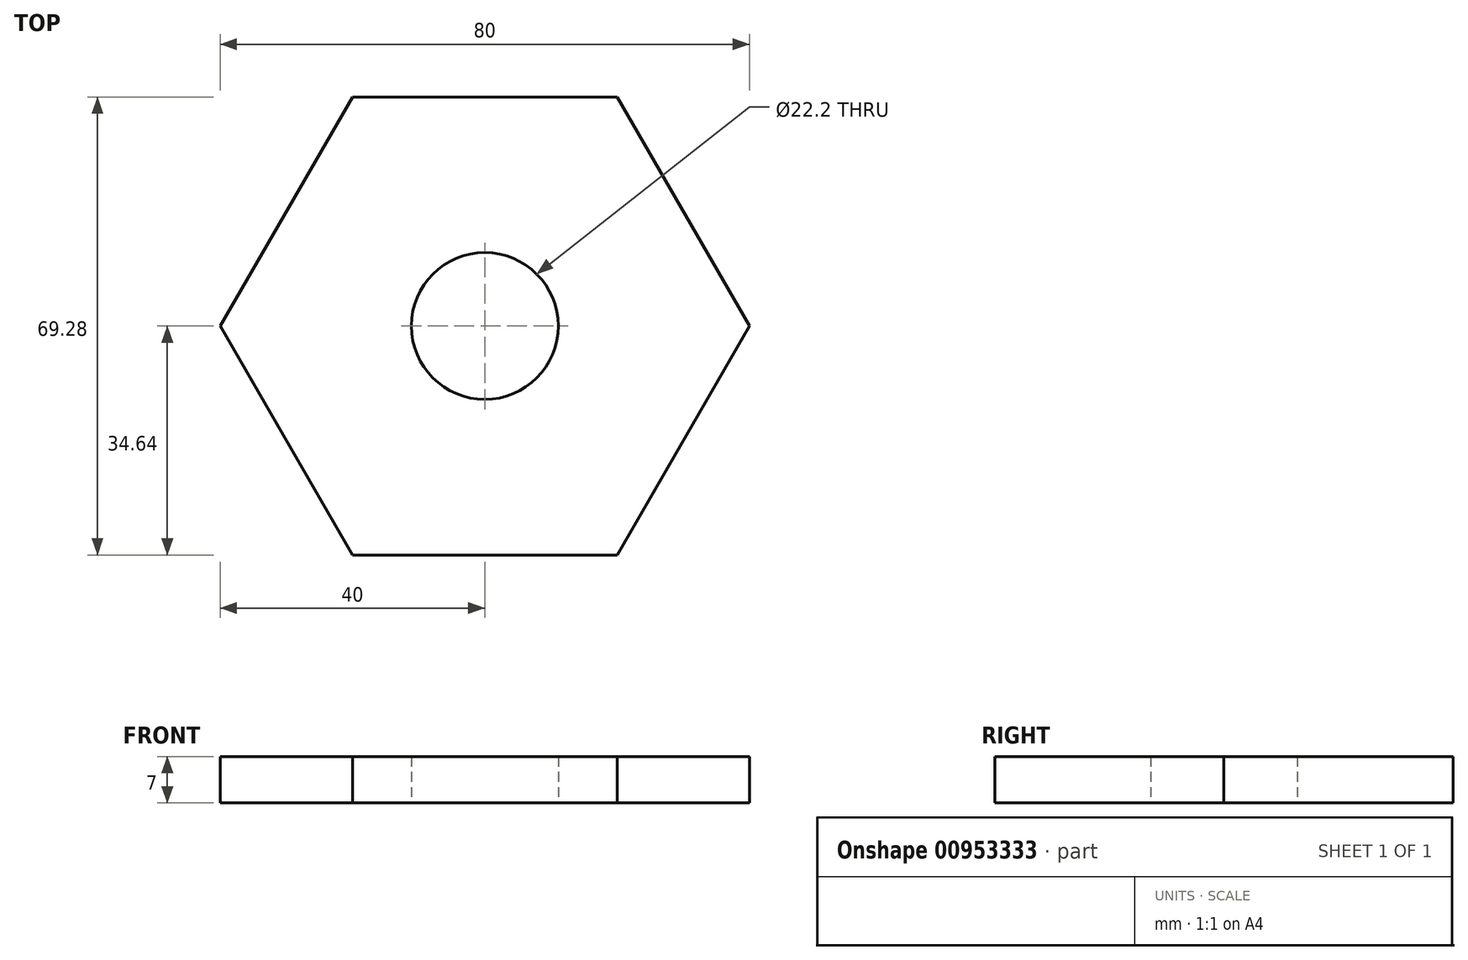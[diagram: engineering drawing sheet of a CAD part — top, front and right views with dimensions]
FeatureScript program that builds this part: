
annotation { "Feature Type Name" : "Feature", "Feature Type Description" : "" }
export const myFeature = defineFeature(function(context is Context, id is Id, definition is map)
    precondition{}
    {
        {
            var Q0;
            Q0=qCreatedBy(makeId("Top.planeOp"),FACE);
            var sketch = newSketch(context, id + "F0", { "sketchPlane" : qUnion([Q0])});
            skCircle(sketch, "E0", {"center": v(0, 0) * mm, "radius": 11.1 * mm});
            skCircle(sketch, "E1.cCircle", {"center": v(0, 0) * mm, "radius": 40 * mm, "construction": true});
            skLineSegment(sketch, "E1.0", {"start": v(40, 0) * mm, "end": v(20, -34.64) * mm});
            skLineSegment(sketch, "E1.1", {"start": v(20, -34.64) * mm, "end": v(-20, -34.64) * mm});
            skLineSegment(sketch, "E1.2", {"start": v(-20, -34.64) * mm, "end": v(-40, 0) * mm});
            skLineSegment(sketch, "E1.3", {"start": v(-40, 0) * mm, "end": v(-20, 34.64) * mm});
            skLineSegment(sketch, "E1.4", {"start": v(-20, 34.64) * mm, "end": v(20, 34.64) * mm});
            skLineSegment(sketch, "E1.5", {"start": v(20, 34.64) * mm, "end": v(40, 0) * mm});
            skLineSegment(sketch, "E2.0", {"start": v(34.5, 3.17) * mm, "end": v(14.5, -31.47) * mm});
            skSolve(sketch);
        }
        {
            var Q0;
            Q0=makeQuery(id+"F0.imprint","IMPRINT",FACE,{"disambiguationData":[TD([[makeQuery(id+"F0.imprint","IMPRINT",EDGE,{"derivedFrom":sQuery(id+"F0.wireOp",EDGE,"E0")}),-1.0]])]});
            extrude(context, id + "F1", {"entities" : qUnion([Q0]), "depth" : 7 * mm, "offsetDistance" : 25 * mm});
        }
    });
